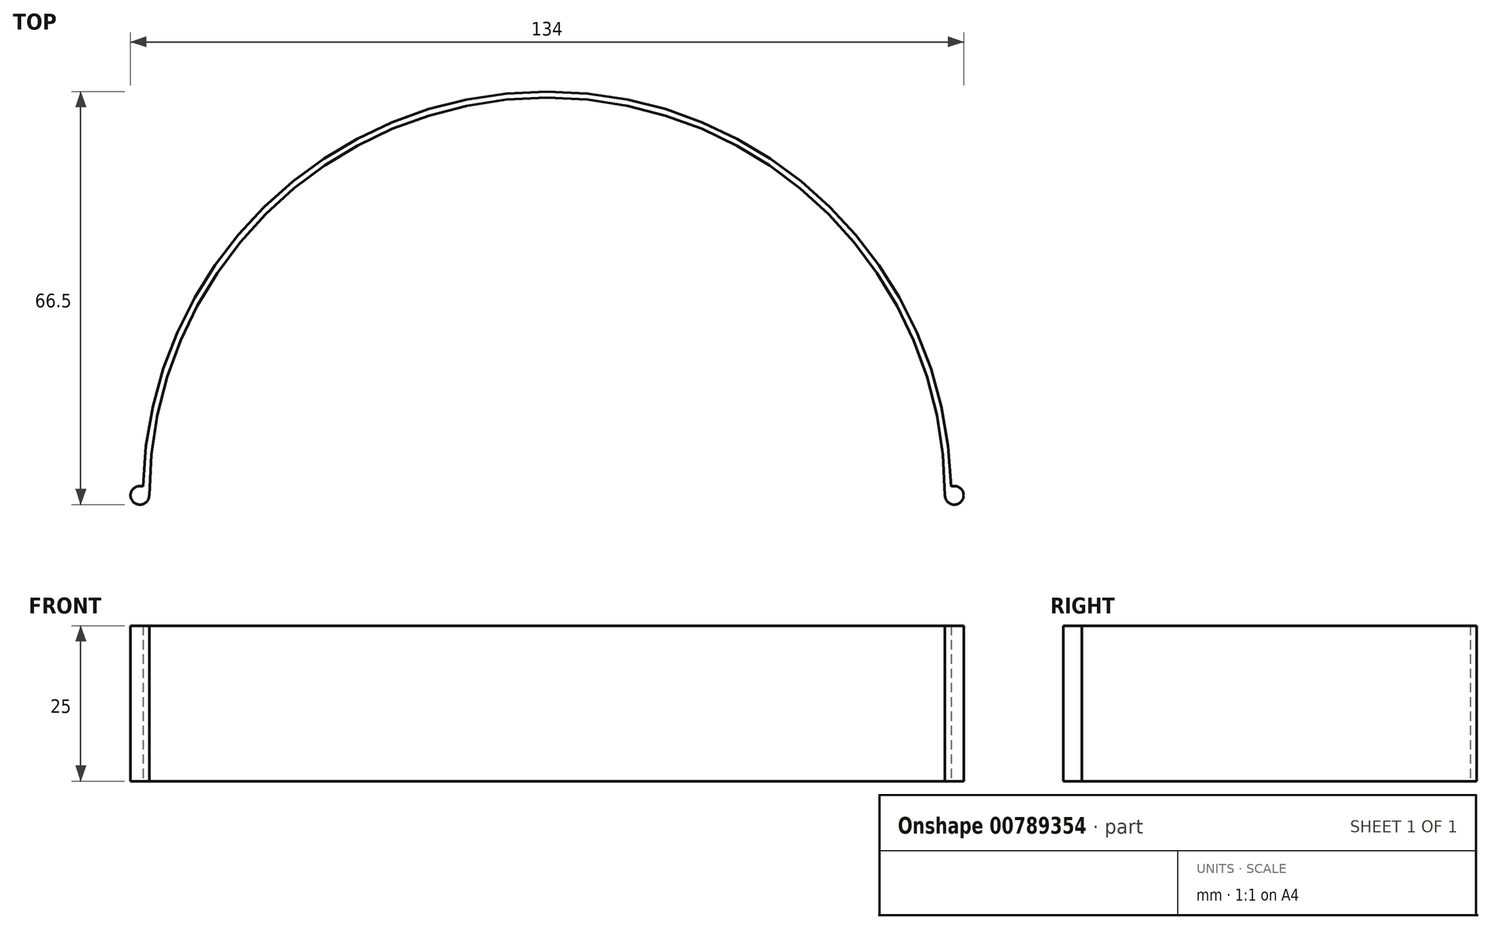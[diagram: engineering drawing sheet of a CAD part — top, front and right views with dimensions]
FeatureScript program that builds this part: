
annotation { "Feature Type Name" : "Feature", "Feature Type Description" : "" }
export const myFeature = defineFeature(function(context is Context, id is Id, definition is map)
    precondition{}
    {
        {
            var Q0;
            Q0=qCreatedBy(makeId("Top.planeOp"),FACE);
            var sketch = newSketch(context, id + "F0", { "sketchPlane" : qUnion([Q0])});
            skCircle(sketch, "E0", {"center": v(0, 0) * mm, "radius": 65 * mm});
            skCircle(sketch, "E1", {"center": v(0, 0) * mm, "radius": 64 * mm});
            skCircle(sketch, "E2", {"center": v(-65.5, 0) * mm, "radius": 1.5 * mm});
            skCircle(sketch, "E3.MirrorC", {"center": v(65.5, 0) * mm, "radius": 1.5 * mm});
            skSolve(sketch);
        }
        {
            var Q0;
            {var subQ0=sQuery(id+"F0.wireOp",EDGE,"E2");var subQ1=sQuery(id+"F0.wireOp",EDGE,"E0");var subQ2=makeQuery(id+"F0.imprint","INTERSECT",VERTEX,{"disambiguationData":[OD(0.0)],"derivedFrom":[subQ1,subQ0]});Q0=makeQuery(id+"F0.imprint","IMPRINT",FACE,{"disambiguationData":[TD([[makeQuery(id+"F0.imprint","IMPRINT",EDGE,{"disambiguationData":[TD([[subQ2,1.0]])],"derivedFrom":subQ1}),1.0]])]});}
            var Q1;
            {var subQ0=sQuery(id+"F0.wireOp",EDGE,"E2");var subQ1=sQuery(id+"F0.wireOp",EDGE,"E0");var subQ2=makeQuery(id+"F0.imprint","INTERSECT",VERTEX,{"disambiguationData":[OD(0.0)],"derivedFrom":[subQ1,subQ0]});Q1=makeQuery(id+"F0.imprint","IMPRINT",FACE,{"disambiguationData":[TD([[makeQuery(id+"F0.imprint","IMPRINT",EDGE,{"disambiguationData":[TD([[subQ2,-1.0]])],"derivedFrom":subQ1}),1.0]])]});}
            var Q2;
            {var subQ0=sQuery(id+"F0.wireOp",EDGE,"E2");var subQ1=sQuery(id+"F0.wireOp",EDGE,"E0");var subQ2=makeQuery(id+"F0.imprint","INTERSECT",VERTEX,{"disambiguationData":[OD(0.0)],"derivedFrom":[subQ1,subQ0]});Q2=makeQuery(id+"F0.imprint","IMPRINT",FACE,{"disambiguationData":[TD([[makeQuery(id+"F0.imprint","IMPRINT",EDGE,{"disambiguationData":[TD([[subQ2,-1.0]])],"derivedFrom":subQ1}),-1.0]])]});}
            var Q3;
            {var subQ0=sQuery(id+"F0.wireOp",EDGE,"E3.MirrorC");var subQ1=sQuery(id+"F0.wireOp",EDGE,"E0");var subQ2=makeQuery(id+"F0.imprint","INTERSECT",VERTEX,{"disambiguationData":[OD(0.0)],"derivedFrom":[subQ1,subQ0]});Q3=makeQuery(id+"F0.imprint","IMPRINT",FACE,{"disambiguationData":[TD([[makeQuery(id+"F0.imprint","IMPRINT",EDGE,{"disambiguationData":[TD([[subQ2,1.0]])],"derivedFrom":subQ1}),-1.0]])]});}
            var Q4;
            {var subQ0=sQuery(id+"F0.wireOp",EDGE,"E3.MirrorC");var subQ1=sQuery(id+"F0.wireOp",EDGE,"E0");var subQ2=makeQuery(id+"F0.imprint","INTERSECT",VERTEX,{"disambiguationData":[OD(0.0)],"derivedFrom":[subQ1,subQ0]});Q4=makeQuery(id+"F0.imprint","IMPRINT",FACE,{"disambiguationData":[TD([[makeQuery(id+"F0.imprint","IMPRINT",EDGE,{"disambiguationData":[TD([[subQ2,1.0]])],"derivedFrom":subQ1}),1.0]])]});}
            extrude(context, id + "F1", {"entities" : qUnion([Q0, Q1, Q2, Q3, Q4]), "depth" : 25 * mm, "offsetDistance" : 25 * mm});
        }
    });
